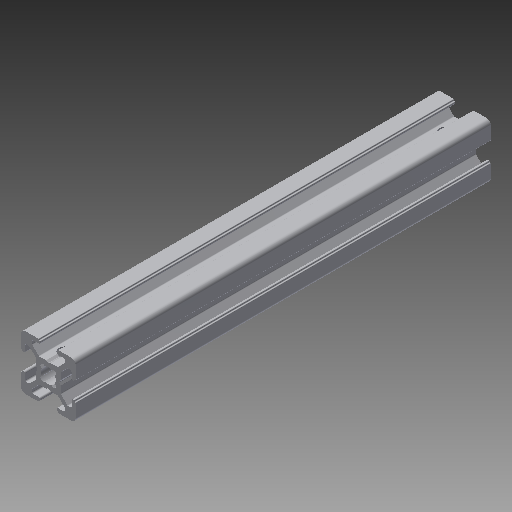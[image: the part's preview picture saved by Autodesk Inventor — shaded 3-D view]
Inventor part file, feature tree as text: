
AUTODESK INVENTOR PART (.ipt)
format: ipt  version: 2017 (Build 210142000, 142)  size: 413,184 bytes
history: native  units: in
note: dims shown in document units (in); Inventor stores cm internally (conversion verified against a paired STEP export)
features: other x3, sketch x2, extrude x1, hole x1, mirror x1
ambient origin geometry x8: Origin, YZ Plane, XZ Plane, XY Plane, X Axis, Y Axis, Z Axis, Center Point
bodies: Solid1 (feature_tree)
feature tree (8):
  other  "Blocks"
  extrude  "Extrusion1"  Depth=0.25in
  hole  "Hole1"  [1 undecoded]
  mirror  "Mirror1"
  sketch  "Sketch1"  dims[d1=0.0in d5=0.25in]
  other  "20x20"
  sketch  "Sketch3"  dims[d6=0.187in d7=0.75in d8=0.375in d9=0.25in d10=0.5635in d11=1.0in d12=0.8108in d13=1.0in d14=1.0in]
  other  "20x20:1"
note: 1 required parameter value undecoded (feature->parameter linkage not recoverable at this tier; creation-order binding heuristic only, values carry confidence <= 0.55)
